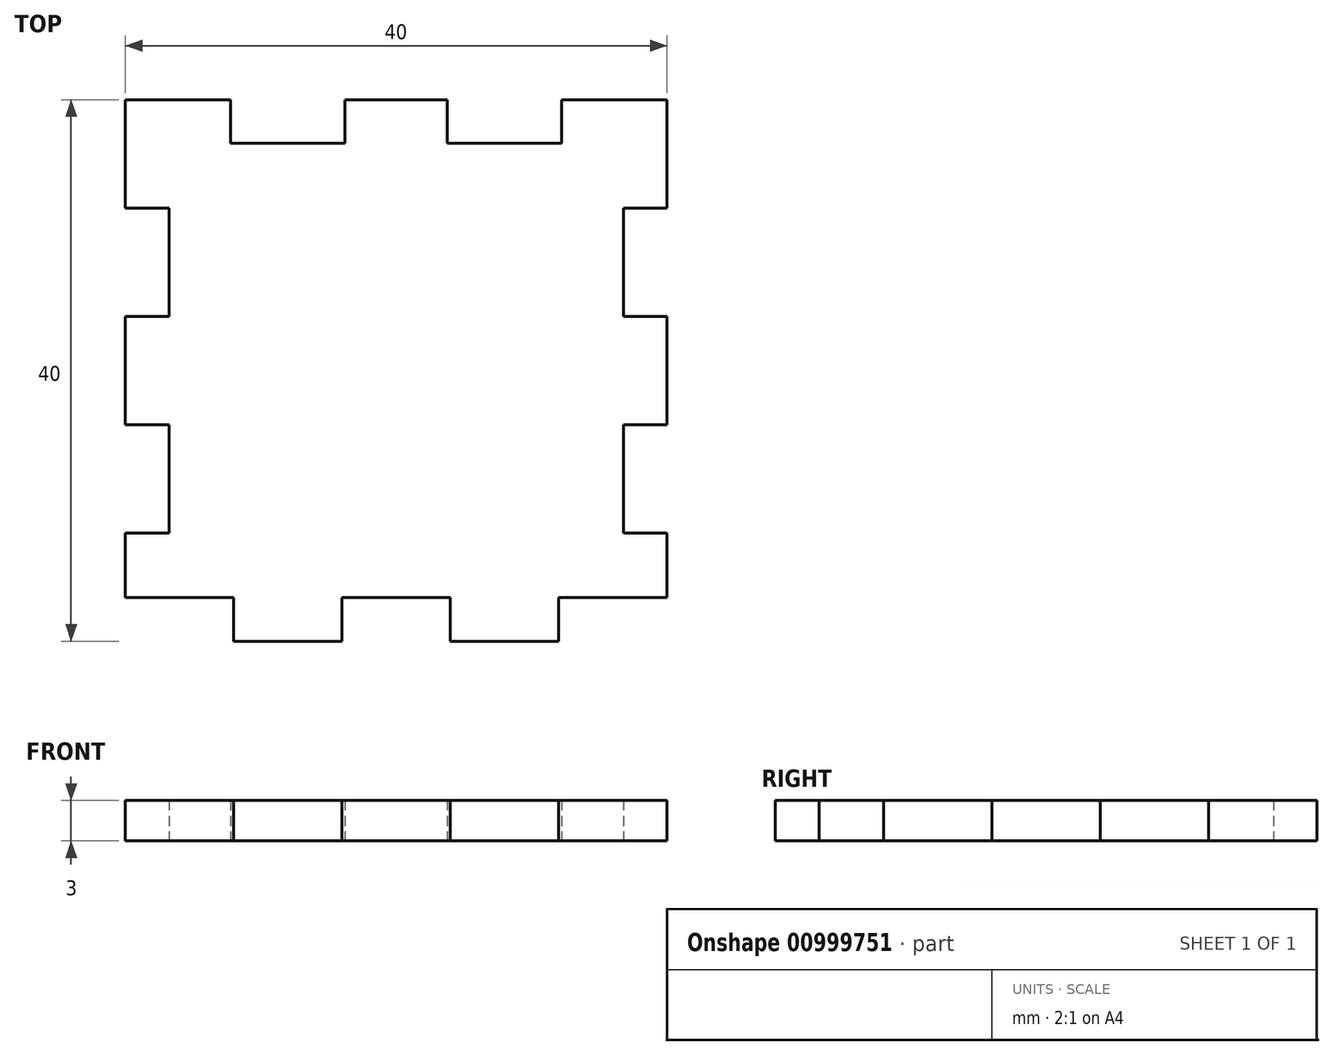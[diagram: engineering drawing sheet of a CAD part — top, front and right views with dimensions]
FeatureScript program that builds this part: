
annotation { "Feature Type Name" : "Feature", "Feature Type Description" : "" }
export const myFeature = defineFeature(function(context is Context, id is Id, definition is map)
    precondition{}
    {
        {
            var Q0;
            Q0=qCreatedBy(makeId("Top.planeOp"),FACE);
            var sketch = newSketch(context, id + "F0", { "sketchPlane" : qUnion([Q0])});
            skLineSegment(sketch, "E0.bottom", {"start": v(20, -20) * mm, "end": v(-20, -20) * mm});
            skLineSegment(sketch, "E0.top", {"start": v(20, 20) * mm, "end": v(-20, 20) * mm});
            skLineSegment(sketch, "E0.left", {"start": v(20, -20) * mm, "end": v(20, 20) * mm});
            skLineSegment(sketch, "E0.right", {"start": v(-20, -20) * mm, "end": v(-20, 20) * mm});
            skPoint(sketch, "E0.middle", {"position": v(0, 0) * mm});
            skSolve(sketch);
        }
        {
            var Q0;
            Q0 = qSketchRegion(id + "F0", true);
            extrude(context, id + "F1", {"entities" : qUnion([Q0]), "depth" : 3 * mm, "offsetDistance" : 25 * mm});
        }
        {
            var Q0;
            Q0=makeQuery(id+"F1.opExtrude","CAP_FACE",FACE,{"disambiguationData":[OSD([sQuery(id+"F0.wireOp",EDGE,"E0.bottom"),sQuery(id+"F0.wireOp",EDGE,"E0.top"),sQuery(id+"F0.wireOp",EDGE,"E0.left"),sQuery(id+"F0.wireOp",EDGE,"E0.right")])],"isStart":true});
            var sketch = newSketch(context, id + "F2", { "sketchPlane" : qUnion([Q0])});
            skLineSegment(sketch, "E1.right", {"start": v(-12, -20) * mm, "end": v(-12, -17) * mm});
            skLineSegment(sketch, "E2.1.0.0", {"start": v(-12, -20) * mm, "end": v(-4, -20) * mm});
            skLineSegment(sketch, "E2.1.0.1", {"start": v(-4, -20) * mm, "end": v(-4, -17) * mm});
            skLineSegment(sketch, "E2.1.0.2", {"start": v(-4, -17) * mm, "end": v(-12, -17) * mm});
            skLineSegment(sketch, "E2.2.0.1", {"start": v(4, -20) * mm, "end": v(4, -17) * mm});
            skLineSegment(sketch, "E2.3.0.0", {"start": v(4, -20) * mm, "end": v(12, -20) * mm});
            skLineSegment(sketch, "E2.3.0.1", {"start": v(12, -20) * mm, "end": v(12, -17) * mm});
            skLineSegment(sketch, "E2.3.0.2", {"start": v(4, -17) * mm, "end": v(12, -17) * mm});
            skLineSegment(sketch, "E3.MirrorCS", {"start": v(20, 20) * mm, "end": v(20, 17) * mm});
            skLineSegment(sketch, "E4.MirrorCS", {"start": v(12, 17) * mm, "end": v(20, 17) * mm});
            skLineSegment(sketch, "E5.MirrorCS", {"start": v(12, 20) * mm, "end": v(20, 20) * mm});
            skLineSegment(sketch, "E6.MirrorCS", {"start": v(12, 20) * mm, "end": v(12, 17) * mm});
            skLineSegment(sketch, "E7.MirrorCS", {"start": v(-4, 17) * mm, "end": v(4, 17) * mm});
            skLineSegment(sketch, "E8.MirrorCS", {"start": v(4, 20) * mm, "end": v(4, 17) * mm});
            skLineSegment(sketch, "E9.MirrorCS", {"start": v(-4, 20) * mm, "end": v(4, 20) * mm});
            skLineSegment(sketch, "E10.MirrorCS", {"start": v(-4, 20) * mm, "end": v(-4, 17) * mm});
            skLineSegment(sketch, "E11.MirrorCS", {"start": v(-12, 20) * mm, "end": v(-12, 17) * mm});
            skLineSegment(sketch, "E12.MirrorCS", {"start": v(-20, 17) * mm, "end": v(-12, 17) * mm});
            skLineSegment(sketch, "E13.MirrorCS", {"start": v(-20, 20) * mm, "end": v(-20, 17) * mm});
            skLineSegment(sketch, "E14.MirrorCS", {"start": v(-20, 20) * mm, "end": v(-12, 20) * mm, "construction": true});
            skLineSegment(sketch, "E15.bottom", {"start": v(-20, -12) * mm, "end": v(-17, -12) * mm});
            skLineSegment(sketch, "E15.top", {"start": v(-20, -4) * mm, "end": v(-17, -4) * mm});
            skLineSegment(sketch, "E15.left", {"start": v(-20, -12) * mm, "end": v(-20, -4) * mm});
            skLineSegment(sketch, "E15.right", {"start": v(-17, -12) * mm, "end": v(-17, -4) * mm});
            skLineSegment(sketch, "E16.MirrorCS", {"start": v(-20, 4) * mm, "end": v(-17, 4) * mm});
            skLineSegment(sketch, "E17.MirrorCS", {"start": v(-20, 12) * mm, "end": v(-20, 4) * mm});
            skLineSegment(sketch, "E18.MirrorCS", {"start": v(-20, 12) * mm, "end": v(-17, 12) * mm});
            skLineSegment(sketch, "E19.MirrorCS", {"start": v(-17, 12) * mm, "end": v(-17, 4) * mm});
            skLineSegment(sketch, "E20.MirrorCS", {"start": v(20, -4) * mm, "end": v(17, -4) * mm});
            skLineSegment(sketch, "E21.MirrorCS", {"start": v(20, -12) * mm, "end": v(20, -4) * mm});
            skLineSegment(sketch, "E22.MirrorCS", {"start": v(20, -12) * mm, "end": v(17, -12) * mm});
            skLineSegment(sketch, "E23.MirrorCS", {"start": v(17, -12) * mm, "end": v(17, -4) * mm});
            skLineSegment(sketch, "E24.MirrorCS", {"start": v(20, 4) * mm, "end": v(17, 4) * mm});
            skLineSegment(sketch, "E25.MirrorCS", {"start": v(20, 12) * mm, "end": v(20, 4) * mm});
            skLineSegment(sketch, "E26.MirrorCS", {"start": v(17, 12) * mm, "end": v(17, 4) * mm});
            skLineSegment(sketch, "E27.MirrorCS", {"start": v(20, 12) * mm, "end": v(17, 12) * mm});
            skSolve(sketch);
        }
        {
            var Q0;
            Q0 = qSketchRegion(id + "F2", true);
            var Q1;
            {var subQ0=sQuery(id+"F2.wireOp",EDGE,"E11.MirrorCS");Q1=makeQuery(id+"F2.imprint","IMPRINT",FACE,{"disambiguationData":[TD([[makeQuery(id+"F2.imprint","IMPRINT",EDGE,{"derivedFrom":subQ0}),-1.0]])]});}
            extrude(context, id + "F3", {"entities" : qUnion([Q0, Q1]), "operationType" : NewBodyOperationType.REMOVE, "endBound" : BoundingType.THROUGH_ALL, "oppositeDirection" : true, "depth" : 3 * mm, "offsetDistance" : 25 * mm});
        }
        {
            var Q0;
            Q0=makeQuery(id+"F1.opExtrude","CAP_FACE",FACE,{"disambiguationData":[OSD([sQuery(id+"F0.wireOp",EDGE,"E0.bottom"),sQuery(id+"F0.wireOp",EDGE,"E0.top"),sQuery(id+"F0.wireOp",EDGE,"E0.left"),sQuery(id+"F0.wireOp",EDGE,"E0.right")])],"isStart":true});
            var sketch = newSketch(context, id + "F4", { "sketchPlane" : qUnion([Q0])});
            skLineSegment(sketch, "E28.0", {"start": v(-3.78, -20) * mm, "end": v(-3.78, -16.78) * mm});
            skLineSegment(sketch, "E28.1", {"start": v(-3.78, -16.78) * mm, "end": v(-12.22, -16.78) * mm});
            skLineSegment(sketch, "E28.2", {"start": v(-12.22, -20) * mm, "end": v(-12.22, -16.78) * mm});
            skLineSegment(sketch, "E29", {"start": v(-12.22, -20) * mm, "end": v(-3.78, -20) * mm});
            skLineSegment(sketch, "E30.MirrorCS", {"start": v(3.78, -20) * mm, "end": v(3.78, -16.78) * mm});
            skLineSegment(sketch, "E31.MirrorCS", {"start": v(12.22, -20) * mm, "end": v(3.78, -20) * mm});
            skLineSegment(sketch, "E32.MirrorCS", {"start": v(3.78, -16.78) * mm, "end": v(12.22, -16.78) * mm});
            skLineSegment(sketch, "E33.MirrorCS", {"start": v(12.22, -20) * mm, "end": v(12.22, -16.78) * mm});
            skLineSegment(sketch, "E34.bottom", {"start": v(-20, 17) * mm, "end": v(-12, 17) * mm});
            skLineSegment(sketch, "E34.top", {"start": v(-20, 16.78) * mm, "end": v(-12, 16.78) * mm});
            skLineSegment(sketch, "E34.left", {"start": v(-20, 17) * mm, "end": v(-20, 16.78) * mm});
            skLineSegment(sketch, "E34.right", {"start": v(-12, 17) * mm, "end": v(-12, 16.78) * mm});
            skLineSegment(sketch, "E35.1.0.0", {"start": v(-4, 16.78) * mm, "end": v(4, 16.78) * mm});
            skLineSegment(sketch, "E35.1.0.1", {"start": v(-4, 17) * mm, "end": v(4, 17) * mm});
            skLineSegment(sketch, "E35.1.0.2", {"start": v(4, 17) * mm, "end": v(4, 16.78) * mm});
            skLineSegment(sketch, "E35.1.0.3", {"start": v(-4, 17) * mm, "end": v(-4, 16.78) * mm});
            skLineSegment(sketch, "E35.2.0.0", {"start": v(12, 16.78) * mm, "end": v(20, 16.78) * mm});
            skLineSegment(sketch, "E35.2.0.1", {"start": v(12, 17) * mm, "end": v(20, 17) * mm});
            skLineSegment(sketch, "E35.2.0.2", {"start": v(20, 17) * mm, "end": v(20, 16.78) * mm});
            skLineSegment(sketch, "E35.2.0.3", {"start": v(12, 17) * mm, "end": v(12, 16.78) * mm});
            skLineSegment(sketch, "E35.direction1", {"start": v(-20, 16.78) * mm, "end": v(-4, 16.78) * mm, "construction": true});
            skLineSegment(sketch, "E36.bottom", {"start": v(-17, -4) * mm, "end": v(-16.78, -4) * mm});
            skLineSegment(sketch, "E36.top", {"start": v(-17, -12) * mm, "end": v(-16.78, -12) * mm});
            skLineSegment(sketch, "E36.left", {"start": v(-17, -4) * mm, "end": v(-17, -12) * mm});
            skLineSegment(sketch, "E36.right", {"start": v(-16.78, -4) * mm, "end": v(-16.78, -12) * mm});
            skLineSegment(sketch, "E37.MirrorCS", {"start": v(-17, 12) * mm, "end": v(-16.78, 12) * mm});
            skLineSegment(sketch, "E38.MirrorCS", {"start": v(-17, 4) * mm, "end": v(-16.78, 4) * mm});
            skLineSegment(sketch, "E39.MirrorCS", {"start": v(-17, 4) * mm, "end": v(-17, 12) * mm});
            skLineSegment(sketch, "E40.MirrorCS", {"start": v(-16.78, 4) * mm, "end": v(-16.78, 12) * mm});
            skLineSegment(sketch, "E41.MirrorCS", {"start": v(17, -12) * mm, "end": v(16.78, -12) * mm});
            skLineSegment(sketch, "E42.MirrorCS", {"start": v(17, -4) * mm, "end": v(16.78, -4) * mm});
            skLineSegment(sketch, "E43.MirrorCS", {"start": v(17, 12) * mm, "end": v(16.78, 12) * mm});
            skLineSegment(sketch, "E44.MirrorCS", {"start": v(17, 4) * mm, "end": v(16.78, 4) * mm});
            skLineSegment(sketch, "E45.MirrorCS", {"start": v(17, 4) * mm, "end": v(17, 12) * mm});
            skLineSegment(sketch, "E46.MirrorCS", {"start": v(16.78, -4) * mm, "end": v(16.78, -12) * mm});
            skLineSegment(sketch, "E47.MirrorCS", {"start": v(17, -4) * mm, "end": v(17, -12) * mm});
            skLineSegment(sketch, "E48.MirrorCS", {"start": v(16.78, 4) * mm, "end": v(16.78, 12) * mm});
            skSolve(sketch);
        }
        {
            var Q0;
            Q0 = qSketchRegion(id + "F4", true);
            extrude(context, id + "F5", {"entities" : qUnion([Q0]), "operationType" : NewBodyOperationType.REMOVE, "endBound" : BoundingType.THROUGH_ALL, "oppositeDirection" : true, "depth" : 25 * mm, "offsetDistance" : 25 * mm});
        }
    });
